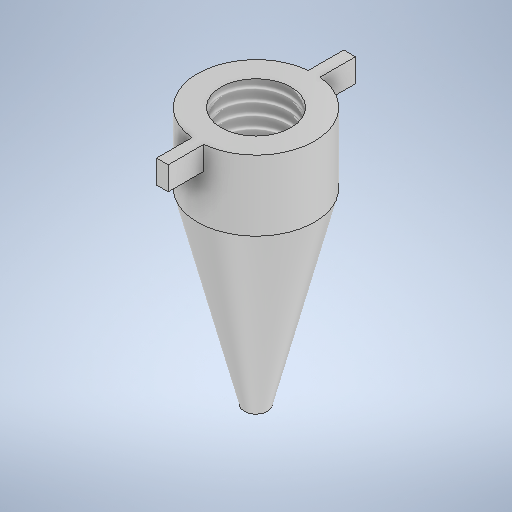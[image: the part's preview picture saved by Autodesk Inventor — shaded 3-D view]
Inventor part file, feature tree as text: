
AUTODESK INVENTOR PART (.ipt)
format: ipt  version: 2025.2 (Build 292293000, 293)  size: 284,160 bytes
history: native  units: mm
features: sketch x1, revolve x1, extrude x1, thread x1
ambient origin geometry x8: Origin, YZ Plane, XZ Plane, XY Plane, X Axis, Y Axis, Z Axis, Center Point
bodies: Solid1 (feature_tree)
feature tree (4):
  sketch  "Sketch1"  dims[d0=1.5mm d1=2.5mm d2=11.0mm d3=0.5mm d4=8.0mm d5=1.0mm d6=1.0mm d7=1.0mm d8=4.0mm d9=1.0mm d10=2.5mm d11=0.1mm d12=90.0deg d13=0.5mm d14=0.0mm d15=3.5mm d16=0.0mm]
  revolve  "Revolution1"  [1 undecoded]
  extrude  "Extrusion1"  Depth=11.0mm
  thread  "Thread1"  [1 undecoded]
note: 2 required parameter values undecoded (feature->parameter linkage not recoverable at this tier; creation-order binding heuristic only, values carry confidence <= 0.55)